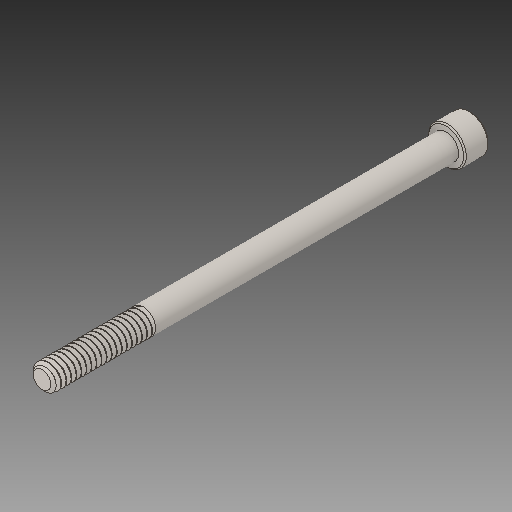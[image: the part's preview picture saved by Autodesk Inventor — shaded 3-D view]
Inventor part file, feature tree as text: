
AUTODESK INVENTOR PART (.ipt)
format: ipt  version: 2017 (Build 210142000, 142)  size: 623,616 bytes
history: native  units: in
note: dims shown in document units (in); Inventor stores cm internally (conversion verified against a paired STEP export)
features: chamfer x1
ambient origin geometry x8: Origin, YZ Plane, XZ Plane, XY Plane, X Axis, Y Axis, Z Axis, Center Point
bodies: Solid1 (feature_tree)
feature tree (1):
  chamfer  "Chamfer2"  [1 undecoded]
note: 1 required parameter value undecoded (feature->parameter linkage not recoverable at this tier; creation-order binding heuristic only, values carry confidence <= 0.55)
